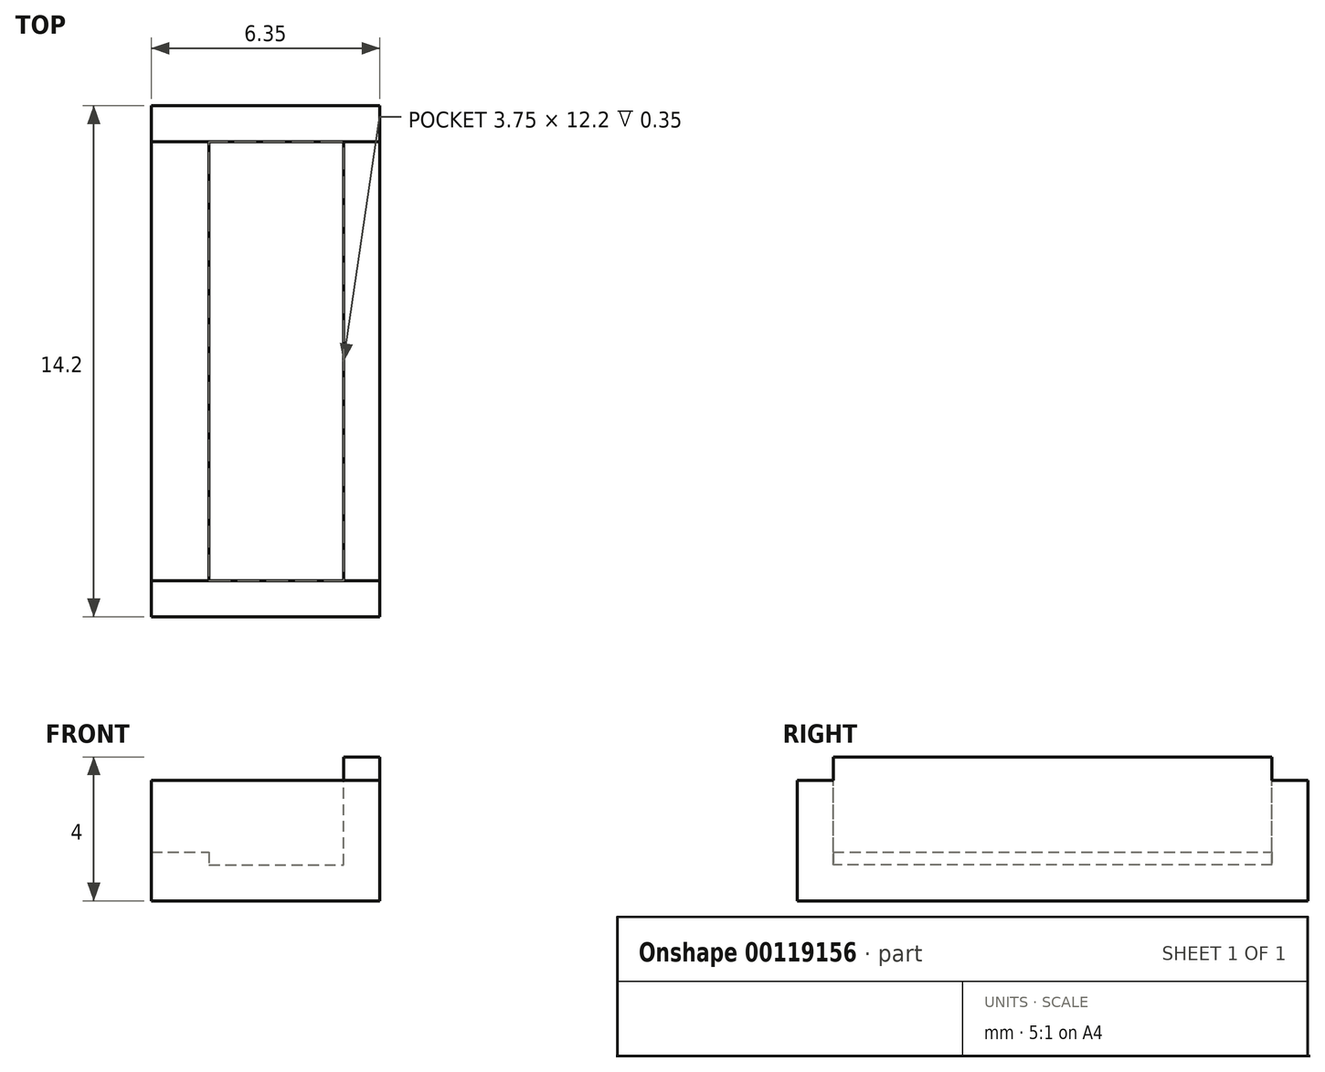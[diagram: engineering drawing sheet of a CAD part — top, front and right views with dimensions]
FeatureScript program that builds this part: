
annotation { "Feature Type Name" : "Feature", "Feature Type Description" : "" }
export const myFeature = defineFeature(function(context is Context, id is Id, definition is map)
    precondition{}
    {
        {
            var Q0;
            Q0=qCreatedBy(makeId("Front.planeOp"),FACE);
            var sketch = newSketch(context, id + "F0", { "sketchPlane" : qUnion([Q0])});
            skLineSegment(sketch, "E0", {"start": v(-2.22, 0) * mm, "end": v(-2.22, 2.65) * mm});
            skLineSegment(sketch, "E1", {"start": v(-2.22, 2.65) * mm, "end": v(-1.62, 2.65) * mm});
            skLineSegment(sketch, "E2", {"start": v(-1.62, 2.65) * mm, "end": v(-1.62, 3) * mm});
            skLineSegment(sketch, "E3", {"start": v(-1.62, 3) * mm, "end": v(2.13, 3) * mm});
            skLineSegment(sketch, "E4", {"start": v(2.13, 3) * mm, "end": v(2.13, 0) * mm});
            skLineSegment(sketch, "E5", {"start": v(2.13, 0) * mm, "end": v(3.13, 0) * mm});
            skLineSegment(sketch, "E6", {"start": v(3.13, 0) * mm, "end": v(3.13, 4) * mm});
            skLineSegment(sketch, "E7", {"start": v(3.13, 4) * mm, "end": v(-3.22, 4) * mm});
            skLineSegment(sketch, "E8", {"start": v(-3.22, 4) * mm, "end": v(-3.22, 0) * mm});
            skLineSegment(sketch, "E9", {"start": v(-3.22, 0) * mm, "end": v(-2.22, 0) * mm});
            skSolve(sketch);
        }
        {
            var Q0;
            Q0 = qSketchRegion(id + "F0", true);
            extrude(context, id + "F1", {"entities" : qUnion([Q0]), "endBound" : BoundingType.SYMMETRIC, "depth" : 12.2 * mm});
        }
        {
            var Q0;
            Q0=makeQuery(id+"F1.opExtrude","SWEPT_FACE",FACE,{"disambiguationData":[OSD([sQuery(id+"F0.wireOp",EDGE,"E9")])]});
            extrude(context, id + "F2", {"entities" : qUnion([Q0]), "operationType" : NewBodyOperationType.REMOVE, "oppositeDirection" : true, "depth" : 0.65 * mm});
        }
        {
            var Q0;
            Q0=makeQuery(id+"F1.opExtrude","CAP_FACE",FACE,{"disambiguationData":[OSD([sQuery(id+"F0.wireOp",EDGE,"E0"),sQuery(id+"F0.wireOp",EDGE,"E1"),sQuery(id+"F0.wireOp",EDGE,"E2"),sQuery(id+"F0.wireOp",EDGE,"E3"),sQuery(id+"F0.wireOp",EDGE,"E4"),sQuery(id+"F0.wireOp",EDGE,"E5"),sQuery(id+"F0.wireOp",EDGE,"E6"),sQuery(id+"F0.wireOp",EDGE,"E7"),sQuery(id+"F0.wireOp",EDGE,"E8"),sQuery(id+"F0.wireOp",EDGE,"E9")])],"isStart":false});
            var sketch = newSketch(context, id + "F3", { "sketchPlane" : qUnion([Q0])});
            skLineSegment(sketch, "E10", {"start": v(-3.22, 0.65) * mm, "end": v(3.13, 0.65) * mm});
            skLineSegment(sketch, "E11", {"start": v(3.13, 0.65) * mm, "end": v(3.13, 4) * mm});
            skLineSegment(sketch, "E12", {"start": v(3.13, 4) * mm, "end": v(-3.22, 4) * mm});
            skLineSegment(sketch, "E13", {"start": v(-3.22, 4) * mm, "end": v(-3.22, 0.65) * mm});
            skSolve(sketch);
        }
        {
            var Q0;
            Q0 = qSketchRegion(id + "F3", true);
            extrude(context, id + "F4", {"entities" : qUnion([Q0]), "operationType" : NewBodyOperationType.ADD, "depth" : 1 * mm});
        }
        {
            var Q0;
            Q0=makeQuery(id+"F1.opExtrude","CAP_FACE",FACE,{"disambiguationData":[OSD([sQuery(id+"F0.wireOp",EDGE,"E0"),sQuery(id+"F0.wireOp",EDGE,"E1"),sQuery(id+"F0.wireOp",EDGE,"E2"),sQuery(id+"F0.wireOp",EDGE,"E3"),sQuery(id+"F0.wireOp",EDGE,"E4"),sQuery(id+"F0.wireOp",EDGE,"E5"),sQuery(id+"F0.wireOp",EDGE,"E6"),sQuery(id+"F0.wireOp",EDGE,"E7"),sQuery(id+"F0.wireOp",EDGE,"E8"),sQuery(id+"F0.wireOp",EDGE,"E9")])],"isStart":true});
            var sketch = newSketch(context, id + "F5", { "sketchPlane" : qUnion([Q0])});
            skLineSegment(sketch, "E14", {"start": v(3.22, 0.65) * mm, "end": v(-3.13, 0.65) * mm});
            skLineSegment(sketch, "E15", {"start": v(-3.13, 0.65) * mm, "end": v(-3.13, 4) * mm});
            skLineSegment(sketch, "E16", {"start": v(-3.13, 4) * mm, "end": v(3.22, 4) * mm});
            skLineSegment(sketch, "E17", {"start": v(3.22, 4) * mm, "end": v(3.22, 0.65) * mm});
            skSolve(sketch);
        }
        {
            var Q0;
            Q0 = qSketchRegion(id + "F5", true);
            extrude(context, id + "F6", {"entities" : qUnion([Q0]), "operationType" : NewBodyOperationType.ADD, "depth" : 1 * mm});
        }
        {
            var Q0;
            Q0=makeQuery(id+"F1.opExtrude","SWEPT_BODY",BODY,{"disambiguationData":[OSD([sQuery(id+"F0.wireOp",EDGE,"E0"),sQuery(id+"F0.wireOp",EDGE,"E1"),sQuery(id+"F0.wireOp",EDGE,"E2"),sQuery(id+"F0.wireOp",EDGE,"E3"),sQuery(id+"F0.wireOp",EDGE,"E4"),sQuery(id+"F0.wireOp",EDGE,"E5"),sQuery(id+"F0.wireOp",EDGE,"E6"),sQuery(id+"F0.wireOp",EDGE,"E7"),sQuery(id+"F0.wireOp",EDGE,"E8"),sQuery(id+"F0.wireOp",EDGE,"E9")])]});
            var Q1;
            Q1=makeQuery(id+"F4.opExtrude","CAP_EDGE",EDGE,{"disambiguationData":[OSD([sQuery(id+"F3.wireOp",EDGE,"E10")])],"isStart":false});
            transform(context, id + "F7", {"entities" : qUnion([Q0]), "transformType" : TransformType.ROTATION, "transformAxis" : qUnion([Q1]), "angle" : 180 * degree, "makeCopy" : false});
        }
        {
            var Q0;
            Q0=makeQuery(id+"F1.opExtrude","SWEPT_FACE",FACE,{"disambiguationData":[OSD([sQuery(id+"F0.wireOp",EDGE,"E0")])]});
            extrude(context, id + "F8", {"entities" : qUnion([Q0]), "operationType" : NewBodyOperationType.REMOVE, "endBound" : BoundingType.UP_TO_NEXT, "oppositeDirection" : true, "depth" : 25 * mm});
        }
    });
